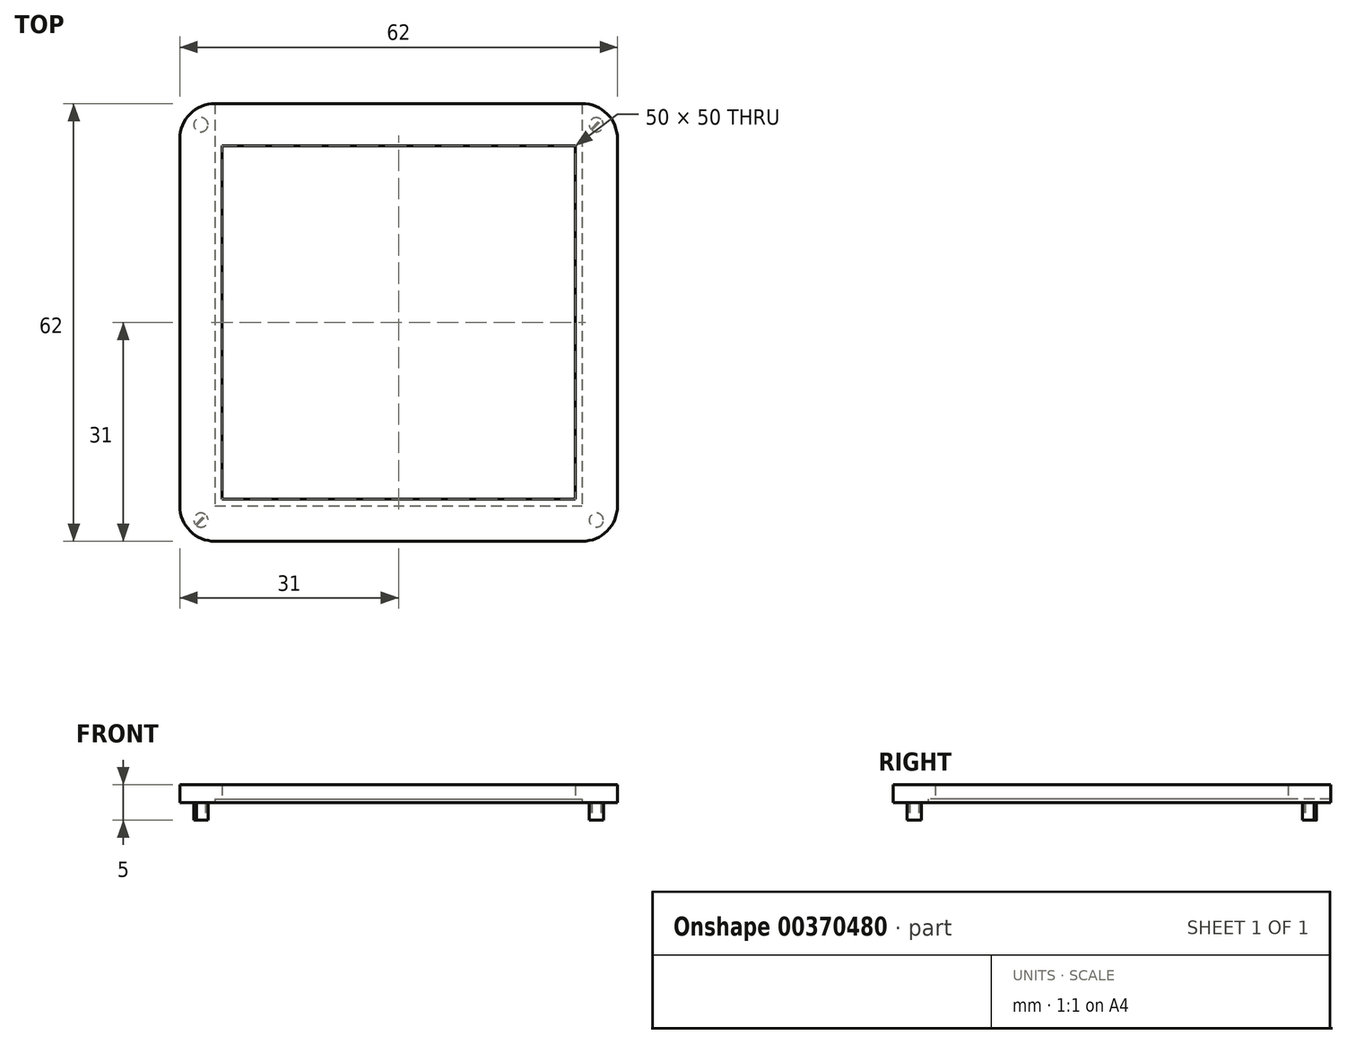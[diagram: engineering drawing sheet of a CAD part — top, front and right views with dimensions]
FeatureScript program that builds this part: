
annotation { "Feature Type Name" : "Feature", "Feature Type Description" : "" }
export const myFeature = defineFeature(function(context is Context, id is Id, definition is map)
    precondition{}
    {
        {
            var Q0;
            Q0=qCreatedBy(makeId("Top.planeOp"),FACE);
            var sketch = newSketch(context, id + "F0", { "sketchPlane" : qUnion([Q0])});
            skLineSegment(sketch, "E0.bottom", {"start": v(5, 0) * mm, "end": v(57, 0) * mm});
            skLineSegment(sketch, "E0.top", {"start": v(5, -62) * mm, "end": v(57, -62) * mm});
            skLineSegment(sketch, "E0.left", {"start": v(0, -5) * mm, "end": v(0, -57) * mm});
            skLineSegment(sketch, "E0.right", {"start": v(62, -5) * mm, "end": v(62, -57) * mm});
            skPoint(sketch, "E1.visualSharp", {"position": v(0, 0) * mm});
            skArc(sketch, "E1.filletArc", {"start": v(5, 0) * mm, "mid": v(1.46, -1.46) * mm, "end": v(0, -5) * mm});
            skPoint(sketch, "E2.visualSharp", {"position": v(62, 0) * mm});
            skArc(sketch, "E2.filletArc", {"start": v(62, -5) * mm, "mid": v(60.54, -1.46) * mm, "end": v(57, 0) * mm});
            skPoint(sketch, "E3.visualSharp", {"position": v(62, -62) * mm});
            skArc(sketch, "E3.filletArc", {"start": v(57, -62) * mm, "mid": v(60.54, -60.54) * mm, "end": v(62, -57) * mm});
            skPoint(sketch, "E4.visualSharp", {"position": v(0, -62) * mm});
            skArc(sketch, "E4.filletArc", {"start": v(0, -57) * mm, "mid": v(1.46, -60.54) * mm, "end": v(5, -62) * mm});
            skLineSegment(sketch, "E5.bottom", {"start": v(5, -5) * mm, "end": v(57, -5) * mm});
            skLineSegment(sketch, "E5.top", {"start": v(5, -57) * mm, "end": v(57, -57) * mm});
            skLineSegment(sketch, "E5.left", {"start": v(5, -5) * mm, "end": v(5, -57) * mm});
            skLineSegment(sketch, "E5.right", {"start": v(57, -5) * mm, "end": v(57, -57) * mm});
            skLineSegment(sketch, "E6.0", {"start": v(6, -6) * mm, "end": v(56, -6) * mm});
            skLineSegment(sketch, "E6.1", {"start": v(6, -6) * mm, "end": v(6, -56) * mm});
            skLineSegment(sketch, "E6.2", {"start": v(6, -56) * mm, "end": v(56, -56) * mm});
            skLineSegment(sketch, "E6.3", {"start": v(56, -6) * mm, "end": v(56, -56) * mm});
            skLineSegment(sketch, "E7", {"start": v(0, 0) * mm, "end": v(6, -6) * mm, "construction": true});
            skPoint(sketch, "E8", {"position": v(3, -3) * mm});
            skLineSegment(sketch, "E9", {"start": v(62, 0) * mm, "end": v(56, -6) * mm, "construction": true});
            skLineSegment(sketch, "E10", {"start": v(62, -62) * mm, "end": v(56, -56) * mm, "construction": true});
            skLineSegment(sketch, "E11", {"start": v(6, -56) * mm, "end": v(0, -62) * mm, "construction": true});
            skCircle(sketch, "E12", {"center": v(3, -3) * mm, "radius": 1 * mm});
            skCircle(sketch, "E13", {"center": v(59, -3) * mm, "radius": 1 * mm});
            skCircle(sketch, "E14", {"center": v(59, -59) * mm, "radius": 1 * mm});
            skCircle(sketch, "E15", {"center": v(3, -59) * mm, "radius": 1 * mm});
            skSolve(sketch);
        }
        {
            var Q0;
            Q0=makeQuery(id+"F0.imprint","IMPRINT",FACE,{"disambiguationData":[TD([[makeQuery(id+"F0.imprint","IMPRINT",EDGE,{"derivedFrom":sQuery(id+"F0.wireOp",EDGE,"E0.bottom")}),-1.0]])]});
            var Q1;
            Q1=makeQuery(id+"F0.imprint","IMPRINT",FACE,{"disambiguationData":[TD([[makeQuery(id+"F0.imprint","IMPRINT",EDGE,{"derivedFrom":sQuery(id+"F0.wireOp",EDGE,"E5.bottom")}),-1.0]])]});
            extrude(context, id + "F1", {"entities" : qUnion([Q0, Q1]), "depth" : 2.5 * mm});
        }
        {
            var Q0;
            Q0=makeQuery(id+"F0.imprint","IMPRINT",FACE,{"disambiguationData":[TD([[makeQuery(id+"F0.imprint","IMPRINT",EDGE,{"derivedFrom":sQuery(id+"F0.wireOp",EDGE,"E5.bottom")}),-1.0]])]});
            extrude(context, id + "F2", {"entities" : qUnion([Q0]), "operationType" : NewBodyOperationType.REMOVE, "depth" : 0.5 * mm});
        }
        {
            var Q0;
            Q0=makeQuery(id+"F0.imprint","IMPRINT",FACE,{"disambiguationData":[TD([[makeQuery(id+"F0.imprint","IMPRINT",EDGE,{"derivedFrom":sQuery(id+"F0.wireOp",EDGE,"E0.bottom")}),-1.0]])]});
            var sketch = newSketch(context, id + "F3", { "sketchPlane" : qUnion([Q0])});
            skLineSegment(sketch, "E16.bottom", {"start": v(5, -5) * mm, "end": v(57, -5) * mm});
            skLineSegment(sketch, "E16.top", {"start": v(5, 0) * mm, "end": v(57, 0) * mm});
            skLineSegment(sketch, "E16.left", {"start": v(5, -5) * mm, "end": v(5, 0) * mm});
            skLineSegment(sketch, "E16.right", {"start": v(57, -5) * mm, "end": v(57, 0) * mm});
            skSolve(sketch);
        }
        {
            var Q0;
            Q0=makeQuery(id+"F3.imprint","IMPRINT",FACE,{"disambiguationData":[TD([[makeQuery(id+"F3.imprint","IMPRINT",EDGE,{"derivedFrom":sQuery(id+"F3.wireOp",EDGE,"E16.bottom")}),1.0]])]});
            extrude(context, id + "F4", {"entities" : qUnion([Q0]), "operationType" : NewBodyOperationType.REMOVE, "depth" : 0.5 * mm});
        }
        {
            var Q0;
            Q0=makeQuery(id+"F0.imprint","IMPRINT",FACE,{"disambiguationData":[TD([[makeQuery(id+"F0.imprint","IMPRINT",EDGE,{"derivedFrom":sQuery(id+"F0.wireOp",EDGE,"E14")}),1.0]])]});
            var Q1;
            Q1=makeQuery(id+"F0.imprint","IMPRINT",FACE,{"disambiguationData":[TD([[makeQuery(id+"F0.imprint","IMPRINT",EDGE,{"derivedFrom":sQuery(id+"F0.wireOp",EDGE,"E13")}),1.0]])]});
            var Q2;
            Q2=makeQuery(id+"F0.imprint","IMPRINT",FACE,{"disambiguationData":[TD([[makeQuery(id+"F0.imprint","IMPRINT",EDGE,{"derivedFrom":sQuery(id+"F0.wireOp",EDGE,"E12")}),1.0]])]});
            var Q3;
            Q3=makeQuery(id+"F0.imprint","IMPRINT",FACE,{"disambiguationData":[TD([[makeQuery(id+"F0.imprint","IMPRINT",EDGE,{"derivedFrom":sQuery(id+"F0.wireOp",EDGE,"E15")}),1.0]])]});
            extrude(context, id + "F5", {"entities" : qUnion([Q0, Q1, Q2, Q3]), "operationType" : NewBodyOperationType.ADD, "depth" : 2.5 * mm, "hasSecondDirection" : true, "secondDirectionOppositeDirection" : true, "secondDirectionDepth" : 2.5 * mm});
        }
        {
            var Q0;
            Q0=makeQuery(id+"F5.opExtrude","CAP_FACE",FACE,{"disambiguationData":[OSD([sQuery(id+"F0.wireOp",EDGE,"E13")])],"isStart":true});
            var sketch = newSketch(context, id + "F6", { "sketchPlane" : qUnion([Q0])});
            skLineSegment(sketch, "E17", {"start": v(58.3, 3.7) * mm, "end": v(59.7, 2.3) * mm, "construction": true});
            skArc(sketch, "E18.0.startCap", {"start": v(58.22, 3.64) * mm, "mid": v(58.22, 3.78) * mm, "end": v(58.36, 3.78) * mm});
            skArc(sketch, "E18.0.endCap", {"start": v(59.78, 2.36) * mm, "mid": v(59.78, 2.22) * mm, "end": v(59.64, 2.22) * mm});
            skLineSegment(sketch, "E18.0.left", {"start": v(58.36, 3.78) * mm, "end": v(59.78, 2.36) * mm});
            skLineSegment(sketch, "E18.0.right", {"start": v(58.22, 3.64) * mm, "end": v(59.64, 2.22) * mm});
            skArc(sketch, "E19.0.startCap", {"start": v(58.22, 3.64) * mm, "mid": v(58.22, 3.78) * mm, "end": v(58.36, 3.78) * mm, "construction": true});
            skArc(sketch, "E19.0.endCap", {"start": v(59.78, 2.36) * mm, "mid": v(59.78, 2.22) * mm, "end": v(59.64, 2.22) * mm, "construction": true});
            skLineSegment(sketch, "E19.0.left", {"start": v(58.36, 3.78) * mm, "end": v(59.78, 2.36) * mm, "construction": true});
            skLineSegment(sketch, "E19.0.right", {"start": v(58.22, 3.64) * mm, "end": v(59.64, 2.22) * mm, "construction": true});
            skSolve(sketch);
        }
        {
            var Q0;
            {var subQ0=sQuery(id+"F6.wireOp",EDGE,"E18.0.left");var subQ1=makeQuery(id+"F5.opExtrude","CAP_EDGE",EDGE,{"disambiguationData":[OSD([sQuery(id+"F0.wireOp",EDGE,"E13")])],"isStart":true});var subQ2=makeQuery(id+"F6.imprint","INTERSECT",VERTEX,{"disambiguationData":[OD(0.0)],"derivedFrom":[subQ1,subQ0]});Q0=makeQuery(id+"F6.imprint","IMPRINT",FACE,{"disambiguationData":[TD([[makeQuery(id+"F6.imprint","IMPRINT",EDGE,{"disambiguationData":[TD([[subQ2,-1.0]])],"derivedFrom":subQ0}),-1.0]])]});}
            extrude(context, id + "F7", {"entities" : qUnion([Q0]), "operationType" : NewBodyOperationType.REMOVE, "oppositeDirection" : true, "depth" : 2.5 * mm});
        }
        {
            var Q0;
            Q0=makeQuery(id+"F5.opExtrude","CAP_FACE",FACE,{"disambiguationData":[OSD([sQuery(id+"F0.wireOp",EDGE,"E15")])],"isStart":true});
            var sketch = newSketch(context, id + "F8", { "sketchPlane" : qUnion([Q0])});
            skLineSegment(sketch, "E20", {"start": v(2.3, 59.7) * mm, "end": v(3.7, 58.3) * mm, "construction": true});
            skArc(sketch, "E21.0.startCap", {"start": v(2.22, 59.64) * mm, "mid": v(2.22, 59.78) * mm, "end": v(2.36, 59.78) * mm});
            skArc(sketch, "E21.0.endCap", {"start": v(3.78, 58.36) * mm, "mid": v(3.78, 58.22) * mm, "end": v(3.64, 58.22) * mm});
            skLineSegment(sketch, "E21.0.left", {"start": v(2.36, 59.78) * mm, "end": v(3.78, 58.36) * mm});
            skLineSegment(sketch, "E21.0.right", {"start": v(2.22, 59.64) * mm, "end": v(3.64, 58.22) * mm});
            skLineSegment(sketch, "E22", {"start": v(2.3, 2.3) * mm, "end": v(3.7, 3.7) * mm, "construction": true});
            skArc(sketch, "E23.0.startCap", {"start": v(2.36, 2.22) * mm, "mid": v(2.22, 2.22) * mm, "end": v(2.22, 2.36) * mm});
            skArc(sketch, "E23.0.endCap", {"start": v(3.64, 3.78) * mm, "mid": v(3.78, 3.78) * mm, "end": v(3.78, 3.64) * mm});
            skLineSegment(sketch, "E23.0.left", {"start": v(2.22, 2.36) * mm, "end": v(3.64, 3.78) * mm});
            skLineSegment(sketch, "E23.0.right", {"start": v(2.36, 2.22) * mm, "end": v(3.78, 3.64) * mm});
            skLineSegment(sketch, "E24", {"start": v(58.3, 58.3) * mm, "end": v(59.7, 59.7) * mm, "construction": true});
            skArc(sketch, "E25.0.startCap", {"start": v(58.36, 58.22) * mm, "mid": v(58.22, 58.22) * mm, "end": v(58.22, 58.36) * mm});
            skArc(sketch, "E25.0.endCap", {"start": v(59.64, 59.78) * mm, "mid": v(59.78, 59.78) * mm, "end": v(59.78, 59.64) * mm});
            skLineSegment(sketch, "E25.0.left", {"start": v(58.22, 58.36) * mm, "end": v(59.64, 59.78) * mm});
            skLineSegment(sketch, "E25.0.right", {"start": v(58.36, 58.22) * mm, "end": v(59.78, 59.64) * mm});
            skSolve(sketch);
        }
        {
            var Q0;
            Q0=makeQuery(id+"F8.imprint","IMPRINT",FACE,{"disambiguationData":[TD([[makeQuery(id+"F8.imprint","IMPRINT",EDGE,{"derivedFrom":sQuery(id+"F8.wireOp",EDGE,"E25.0.startCap")}),-1.0]])]});
            var Q1;
            Q1=makeQuery(id+"F8.imprint","IMPRINT",FACE,{"disambiguationData":[TD([[makeQuery(id+"F8.imprint","IMPRINT",EDGE,{"derivedFrom":sQuery(id+"F8.wireOp",EDGE,"E23.0.startCap")}),-1.0]])]});
            var Q2;
            {var subQ0=sQuery(id+"F8.wireOp",EDGE,"E21.0.left");var subQ1=makeQuery(id+"F5.opExtrude","CAP_EDGE",EDGE,{"disambiguationData":[OSD([sQuery(id+"F0.wireOp",EDGE,"E15")])],"isStart":true});var subQ2=makeQuery(id+"F8.imprint","INTERSECT",VERTEX,{"disambiguationData":[OD(0.0)],"derivedFrom":[subQ1,subQ0]});Q2=makeQuery(id+"F8.imprint","IMPRINT",FACE,{"disambiguationData":[TD([[makeQuery(id+"F8.imprint","IMPRINT",EDGE,{"disambiguationData":[TD([[subQ2,-1.0]])],"derivedFrom":subQ0}),-1.0]])]});}
            extrude(context, id + "F9", {"entities" : qUnion([Q0, Q1, Q2]), "operationType" : NewBodyOperationType.REMOVE, "oppositeDirection" : true, "depth" : 2.5 * mm});
        }
    });
